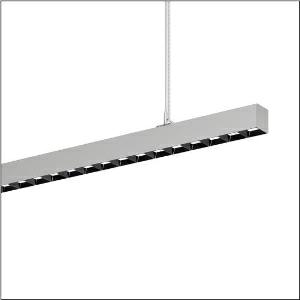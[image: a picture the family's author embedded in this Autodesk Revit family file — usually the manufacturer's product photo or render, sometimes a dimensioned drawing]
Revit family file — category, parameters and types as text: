
# Revit family: silica_r__21_51mx31dc3dsb_b806
name_source: partatom
category: Lighting Fixtures
units: mm (PartAtom-declared; Revit-internal decimal feet)

## family parameters
Cut with Voids When Loaded = No
Host = Face
Light Source = No
Part Type = Normal
Room Calculation Point = No
Round Connector Dimension = Use Diameter
Shared = No

## types (1)
- --- (1 x LED, 18230 lm, 113.3 W, 3000K)
    Apparent Load = 113 VA
    CIE Flux Codes = 87 99 100 59 100
    Color Rendering = 80
    Color Temperature = 3000K
    Default Elevation = 1800 mm
    Description = Silica® 21, office luminaire, primary light control with darklight reflector, of PMMA, black, CAT 2 (L<= 3000cd/m²), light emission: direct/indirect distribution, primary light characteristic: symmetric, installation type: suspended mounting, LED, rated luminous flux: 18.230lm, luminous efficacy: 161lm/W, light colour: 830, colour temperature: 3000K, with terminal, 3+2-pole, max. 2.5mm², mains connection: 220..240V, AC, 50/60Hz, rated input power: 113.3W, luminaire housing, of aluminium, metallic grey (RAL 9006), length: 3.004mm, width: 53mm, height: 53mm, protection rating (complete): IP20, insulation class (complete): insulation class I (protective earthing), certification: CE, permissible operating ambient temperature: 0..+35°C, standard: EN 50419, packaging unit: 1 piece
    Height = 53 mm
    Lamp = 1 x LED
    Lamp Light Flux = 18230 lm
    Lamp Power = 113.3 W
    Lamp count = 1
    Length = 3004 mm
    Luminous efficacy = 161 lm/W
    Manufacturer = Siteco
    ModVariant = No
    Model = 51MX31DC3DSB
    Mounting Place = Ceiling
    Mounting Type = Pendant
    Number of Poles = 1
    OnlyDefault = Yes
    Power Factor = 1
    Product Name = Silica® 21
    Product group = office luminaire | ceiling pendant
    ProductGroupID = 902
    Protection Class = Protection class I
    Protection Degree = IP 20
    RLX_Detail_Level = 1
    RLX_Emergency_Light_Flux = 0 lm
    RLX_Emergency_Type = 0
    RLX_Emergency_Type_DB = No
    RlxData = <blob elided: 65417 chars, md5=18ccabf2>
    Socket = socket
    Standby Power = 0 W
    System Light Flux = 18230 lm
    System Power = 113 W
    Type Comments = factory setting: luminous flux: 100 % | dim-lin: 254 | 392 mA
    Type Image = l_1313642.jpg
    URL = http://relux.com
    VarID = @adj_069787
    Voltage = 0 V
    Weight = 0.00 kg
    Width = 53 mm

## geometry (parser evidence)
native form markers: Blend x4, Sweep x13
no freeform markers — native parametric forms only
